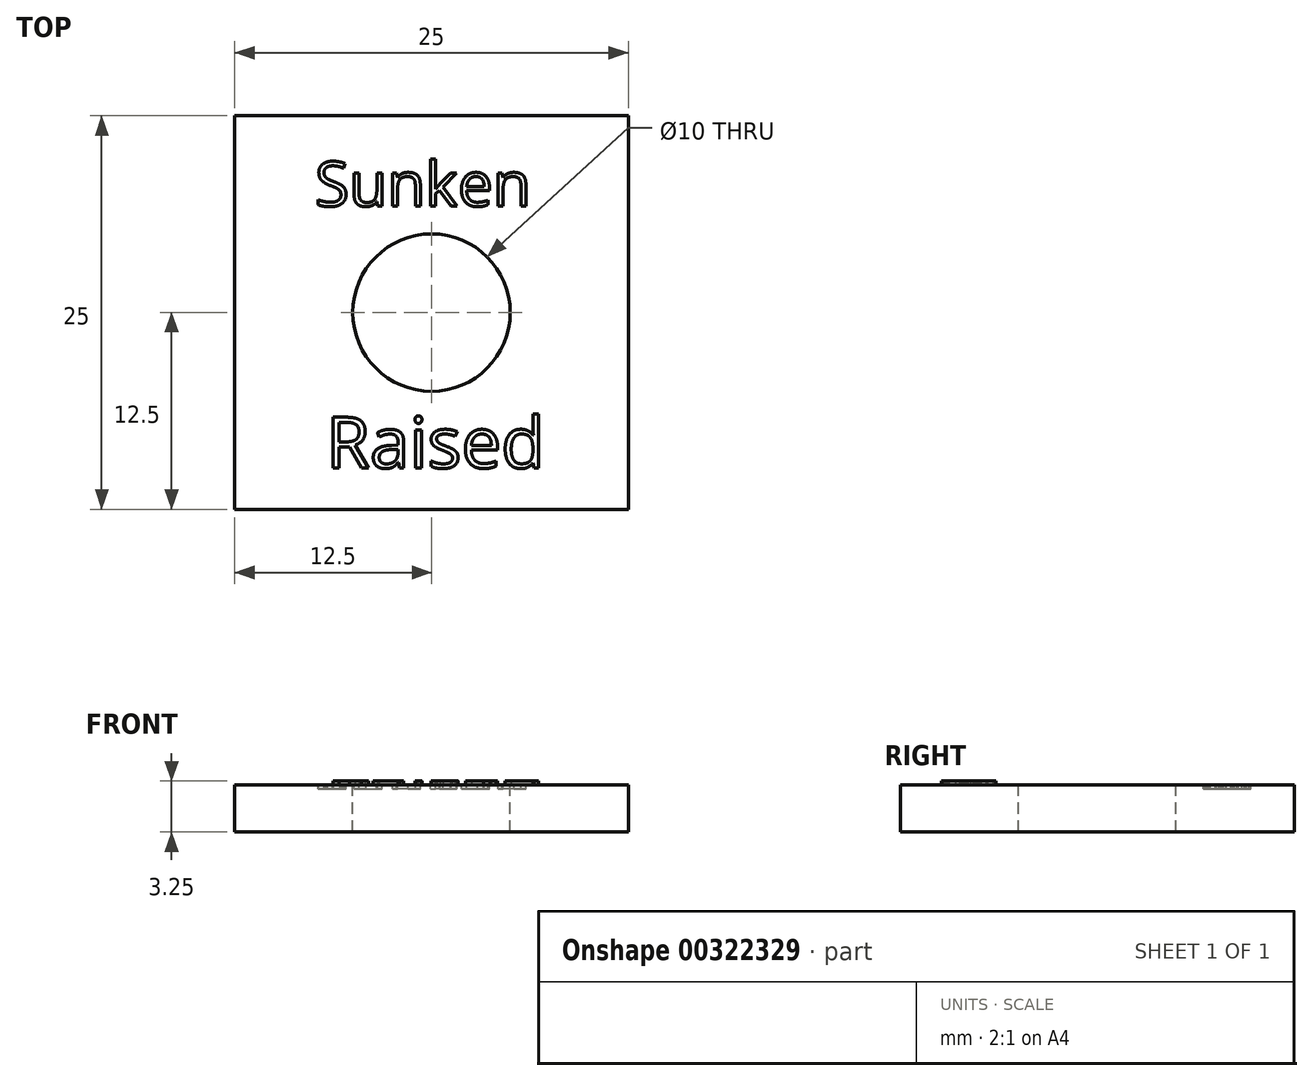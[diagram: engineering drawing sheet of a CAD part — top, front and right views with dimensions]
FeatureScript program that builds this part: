
annotation { "Feature Type Name" : "Feature", "Feature Type Description" : "" }
export const myFeature = defineFeature(function(context is Context, id is Id, definition is map)
    precondition{}
    {
        {
            var Q0;
            Q0=qCreatedBy(makeId("Top.planeOp"),FACE);
            var sketch = newSketch(context, id + "F0", { "sketchPlane" : qUnion([Q0])});
            skLineSegment(sketch, "E0.bottom", {"start": v(12.5, 12.5) * mm, "end": v(-12.5, 12.5) * mm});
            skLineSegment(sketch, "E0.top", {"start": v(12.5, -12.5) * mm, "end": v(-12.5, -12.5) * mm});
            skLineSegment(sketch, "E0.left", {"start": v(12.5, 12.5) * mm, "end": v(12.5, -12.5) * mm});
            skLineSegment(sketch, "E0.right", {"start": v(-12.5, 12.5) * mm, "end": v(-12.5, -12.5) * mm});
            skPoint(sketch, "E0.middle", {"position": v(0, 0) * mm});
            skSolve(sketch);
        }
        {
            var Q0;
            Q0=makeQuery(id+"F0.imprint","IMPRINT",FACE,{"disambiguationData":[TD([[makeQuery(id+"F0.imprint","IMPRINT",EDGE,{"derivedFrom":sQuery(id+"F0.wireOp",EDGE,"E0.bottom")}),1.0]])]});
            extrude(context, id + "F1", {"entities" : qUnion([Q0]), "depth" : 3 * mm, "offsetDistance" : 25 * mm});
        }
        {
            var Q0;
            Q0=sQuery(id+"F0.wireOp",VERTEX,"E0.middle");
            var Q1;
            Q1=makeQuery(id+"F1.opExtrude","SWEPT_BODY",BODY,{"disambiguationData":[OSD([sQuery(id+"F0.wireOp",EDGE,"E0.bottom"),sQuery(id+"F0.wireOp",EDGE,"E0.top"),sQuery(id+"F0.wireOp",EDGE,"E0.left"),sQuery(id+"F0.wireOp",EDGE,"E0.right")])]});
            hole(context, id + "F2", {"style" : HoleStyle.SIMPLE, "endStyle" : HoleEndStyle.THROUGH, "oppositeDirection" : true, "holeDiameter" : 10 * mm, "tappedDepth" : 12 * mm, "tapClearance" : 3, "locations" : qUnion([Q0]), "scope" : qUnion([Q1])});
        }
        {
            var Q0;
            Q0=makeQuery(id+"F1.opExtrude","CAP_FACE",FACE,{"disambiguationData":[OSD([sQuery(id+"F0.wireOp",EDGE,"E0.bottom"),sQuery(id+"F0.wireOp",EDGE,"E0.top"),sQuery(id+"F0.wireOp",EDGE,"E0.left"),sQuery(id+"F0.wireOp",EDGE,"E0.right")])],"isStart":false});
            var sketch = newSketch(context, id + "F3", { "sketchPlane" : qUnion([Q0])});
            skText(sketch, "E1", { "text": "Sunken", "fontName": "OpenSans-Regular.ttf"});
            const initialGuessF3  = {"E1": [-0.0074, 0.00676, 1, 0, 0.00284]};
            skSetInitialGuess(sketch, initialGuessF3);
            skSolve(sketch);
        }
        {
            var Q0;
            Q0 = qSketchRegion(id + "F3", true);
            extrude(context, id + "F4", {"entities" : qUnion([Q0]), "operationType" : NewBodyOperationType.REMOVE, "oppositeDirection" : true, "depth" : 0.25 * mm});
        }
        {
            var Q0;
            {var subQ0=sQuery(id+"F0.wireOp",EDGE,"E0.left");var subQ1=sQuery(id+"F0.wireOp",EDGE,"E0.right");var subQ2=sQuery(id+"F0.wireOp",EDGE,"E0.bottom");var subQ3=sQuery(id+"F0.wireOp",EDGE,"E0.top");Q0=makeQuery(id+"F4.boolean.opBoolean","SPLIT",FACE,{"disambiguationData":[TD([makeQuery(id+"F1.opExtrude","SWEPT_FACE",FACE,{"disambiguationData":[OSD([subQ2])]})])],"derivedFrom":makeQuery(id+"F1.opExtrude","CAP_FACE",FACE,{"disambiguationData":[OSD([subQ2,subQ3,subQ0,subQ1])],"isStart":false})});}
            var sketch = newSketch(context, id + "F5", { "sketchPlane" : qUnion([Q0])});
            skText(sketch, "E2", { "text": "Raised", "fontName": "OpenSans-Regular.ttf"});
            const initialGuessF5  = {"E2": [-0.0067, -0.00987, 1, 0, 0.00325]};
            skSetInitialGuess(sketch, initialGuessF5);
            skSolve(sketch);
        }
        {
            var Q0;
            Q0 = qSketchRegion(id + "F5", true);
            extrude(context, id + "F6", {"entities" : qUnion([Q0]), "operationType" : NewBodyOperationType.ADD, "depth" : 0.25 * mm, "offsetDistance" : 25 * mm});
        }
    });
